# Revit family: #window cill
name_source: partatom
category: Detail Items
revit_build: Autodesk Revit 2017 (Build: 20160225_1515(x64)
units: mm (PartAtom-declared; Revit-internal decimal feet)

## family parameters
Rotate with component = No
Section Shape = Not Defined
Shared = No

## types (2) — shared parameters
cill = Yes
facing depth = 8 mm  [stored 0.0262467 ft]
frame rebate depth = 13 mm
frame tolerance = 10 mm  [stored 0.0328084 ft]
frame width = 92 mm  [stored 0.301837 ft]
gl-1 = 16 mm  [stored 0.0524934 ft]
gl-2 = 4 mm  [stored 0.0131234 ft]
gl-3 = 16 mm  [stored 0.0524934 ft]
gl-4 = 6 mm  [stored 0.019685 ft]
profile depth = 61 mm  [stored 0.200131 ft]
profile width = 63 mm  [stored 0.206693 ft]
seal w = 10 mm  [stored 0.0328084 ft]

## per-type parameters (varying)
| type | cill downstand | cill overhang | cill projection minus cill overhang | facing to frame | frame depth | frame gap | gl-5 |
| faced frame type 01 | 20 mm  [stored 0.0656168 ft] | 25 mm  [stored 0.082021 ft] | 75 mm | Yes | 35 mm  [stored 0.114829 ft] | 10 mm  [stored 0.0328084 ft] | 16 mm  [stored 0.0524934 ft] |
| non faced frame 01 | 18 mm | 12 mm  [stored 0.0393701 ft] | 41 mm | No | 38 mm  [stored 0.124672 ft] | 5 mm  [stored 0.0164042 ft] | 10 mm  [stored 0.0328084 ft] |

note: [stored X ft] marks values corroborated as IEEE doubles in the binary element streams (Revit-internal decimal feet)

## geometry (parser evidence)
native form markers: Sweep x1
no freeform markers — native parametric forms only
